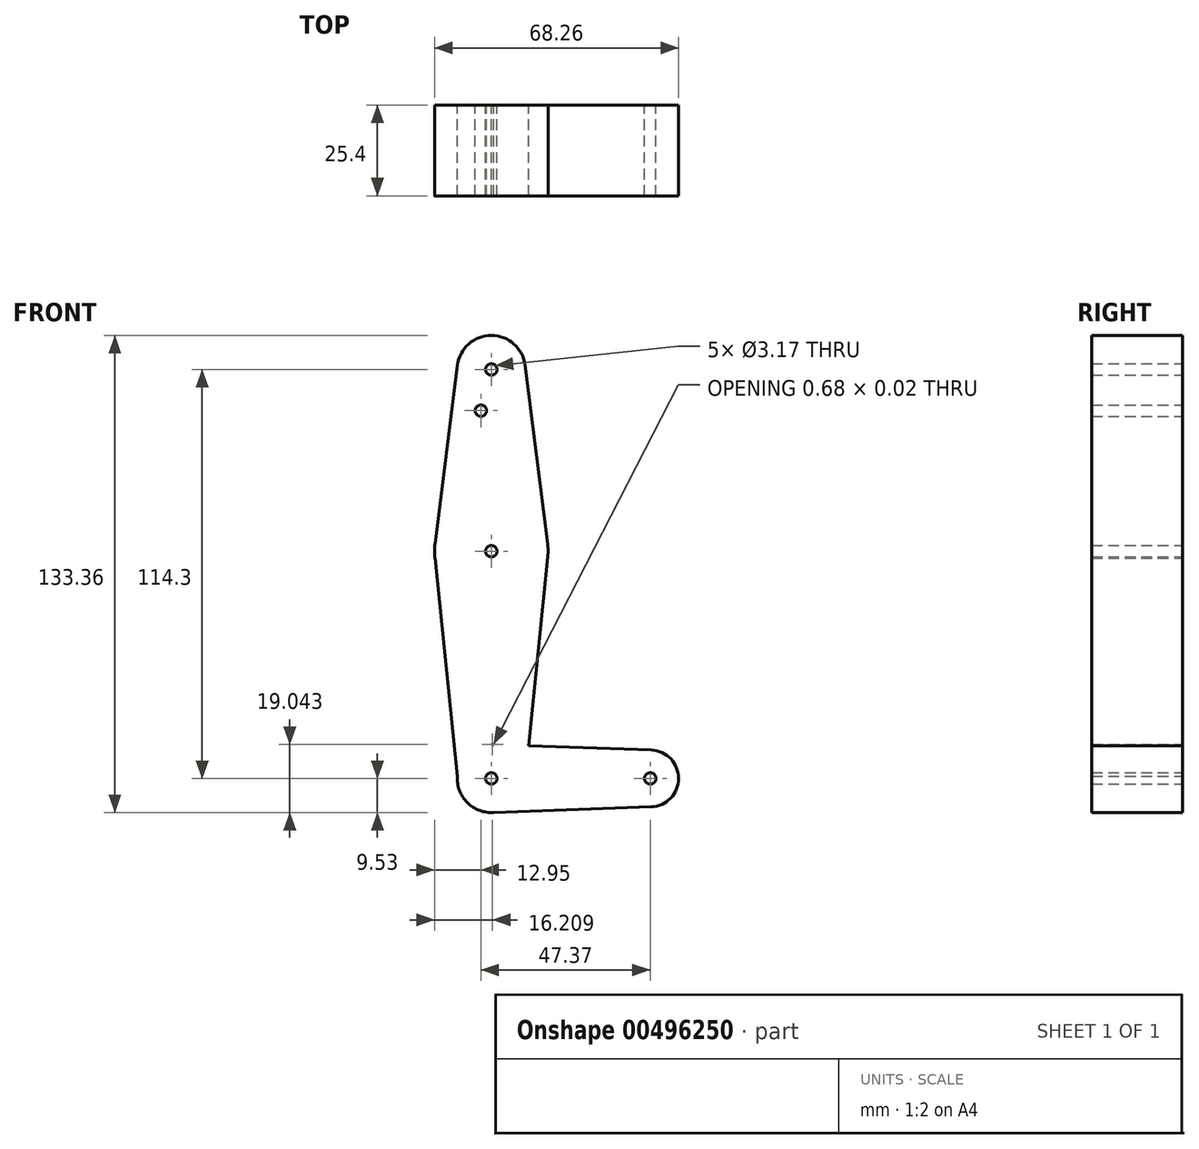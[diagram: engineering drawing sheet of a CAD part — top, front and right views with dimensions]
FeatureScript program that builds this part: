
annotation { "Feature Type Name" : "Feature", "Feature Type Description" : "" }
export const myFeature = defineFeature(function(context is Context, id is Id, definition is map)
    precondition{}
    {
        {
            var Q0;
            Q0=qCreatedBy(makeId("Front.planeOp"),FACE);
            var sketch = newSketch(context, id + "F0", { "sketchPlane" : qUnion([Q0])});
            skLineSegment(sketch, "E0", {"start": v(0, 0) * mm, "end": v(0, 114.3) * mm});
            skLineSegment(sketch, "E1", {"start": v(0, 114.3) * mm, "end": v(0, 0) * mm});
            skLineSegment(sketch, "E2", {"start": v(0, 0) * mm, "end": v(44.45, 0) * mm});
            skCircle(sketch, "E3", {"center": v(0, 114.3) * mm, "radius": 9.53 * mm});
            skCircle(sketch, "E4", {"center": v(0, 0) * mm, "radius": 9.53 * mm});
            skCircle(sketch, "E5", {"center": v(0, 63.5) * mm, "radius": 15.88 * mm});
            skCircle(sketch, "E6", {"center": v(44.45, 0) * mm, "radius": 7.94 * mm});
            skLineSegment(sketch, "E7", {"start": v(-9.45, 115.5) * mm, "end": v(-15.75, 65.48) * mm});
            skLineSegment(sketch, "E8", {"start": v(-15.75, 65.48) * mm, "end": v(-9.45, 115.5) * mm});
            skLineSegment(sketch, "E9", {"start": v(-15.75, 61.52) * mm, "end": v(-9.45, 0) * mm});
            skLineSegment(sketch, "E10", {"start": v(-9.45, 0) * mm, "end": v(-15.75, 61.52) * mm});
            skLineSegment(sketch, "E11", {"start": v(9.45, 115.5) * mm, "end": v(15.76, 65.44) * mm});
            skLineSegment(sketch, "E12", {"start": v(15.76, 65.44) * mm, "end": v(9.45, 115.5) * mm});
            skLineSegment(sketch, "E13", {"start": v(0, 9.53) * mm, "end": v(44.73, 7.93) * mm});
            skLineSegment(sketch, "E14", {"start": v(44.73, 7.93) * mm, "end": v(0, 9.53) * mm});
            skLineSegment(sketch, "E15", {"start": v(0, -9.53) * mm, "end": v(44.73, -7.93) * mm});
            skLineSegment(sketch, "E16", {"start": v(44.73, -7.93) * mm, "end": v(0, -9.53) * mm});
            skLineSegment(sketch, "E17", {"start": v(9.53, 0) * mm, "end": v(15.8, 61.9) * mm});
            skCircle(sketch, "E18", {"center": v(0, 114.3) * mm, "radius": 1.59 * mm});
            skCircle(sketch, "E19", {"center": v(0, 63.5) * mm, "radius": 1.59 * mm});
            skCircle(sketch, "E20", {"center": v(0, 0) * mm, "radius": 1.59 * mm});
            skCircle(sketch, "E21", {"center": v(44.45, 0) * mm, "radius": 1.59 * mm});
            skCircle(sketch, "E22", {"center": v(-2.92, 102.8) * mm, "radius": 1.59 * mm});
            skSolve(sketch);
        }
        {
            var Q0;
            Q0 = qSketchRegion(id + "F0", true);
            var Q1;
            {var subQ3=sQuery(id+"F0.wireOp",EDGE,"E20");var subQ6=sQuery(id+"F0.wireOp",EDGE,"E1");var subQ9=makeQuery(id+"F0.imprint","INTERSECT",VERTEX,{"derivedFrom":[subQ6,subQ3]});Q1=makeQuery(id+"F0.imprint","IMPRINT",FACE,{"disambiguationData":[TD([[makeQuery(id+"F0.imprint","IMPRINT",EDGE,{"disambiguationData":[TD([[subQ9,1.0]])],"derivedFrom":subQ3}),-1.0]])]});}
            extrude(context, id + "F1", {"entities" : qUnion([Q0, Q1]), "depth" : 25.4 * mm});
        }
    });
